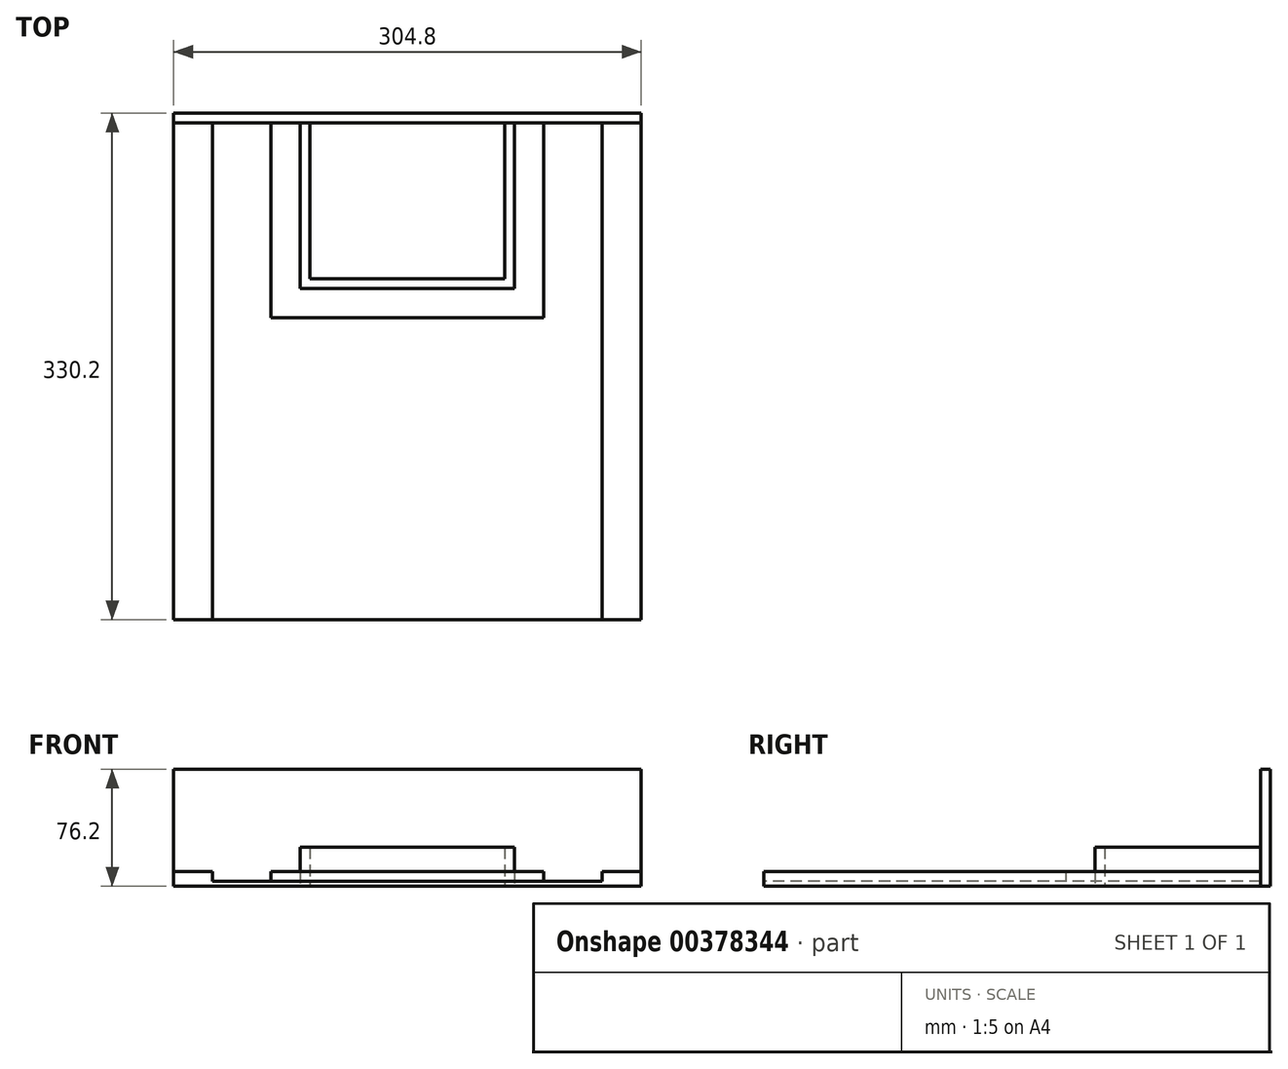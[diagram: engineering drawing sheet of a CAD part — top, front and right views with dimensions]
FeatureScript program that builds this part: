
annotation { "Feature Type Name" : "Feature", "Feature Type Description" : "" }
export const myFeature = defineFeature(function(context is Context, id is Id, definition is map)
    precondition{}
    {
        {
            var Q0;
            Q0=qCreatedBy(makeId("Top.planeOp"),FACE);
            var sketch = newSketch(context, id + "F0", { "sketchPlane" : qUnion([Q0])});
            skLineSegment(sketch, "E0.bottom", {"start": v(152.4, 165.1) * mm, "end": v(-152.4, 165.1) * mm});
            skLineSegment(sketch, "E0.top", {"start": v(152.4, -165.1) * mm, "end": v(-152.4, -165.1) * mm});
            skLineSegment(sketch, "E0.left", {"start": v(152.4, 165.1) * mm, "end": v(152.4, -165.1) * mm});
            skLineSegment(sketch, "E0.right", {"start": v(-152.4, 165.1) * mm, "end": v(-152.4, -165.1) * mm});
            skPoint(sketch, "E0.middle", {"position": v(0, 0) * mm});
            skLineSegment(sketch, "E1.0", {"start": v(152.4, 158.75) * mm, "end": v(-152.4, 158.75) * mm});
            skLineSegment(sketch, "E2.0", {"start": v(-127, 158.75) * mm, "end": v(-127, -165.1) * mm});
            skLineSegment(sketch, "E3.0", {"start": v(127, 158.75) * mm, "end": v(127, -165.1) * mm});
            skPoint(sketch, "E4", {"position": v(0, 158.75) * mm});
            skLineSegment(sketch, "E5", {"start": v(0, 158.75) * mm, "end": v(0, 0) * mm, "construction": true});
            skPoint(sketch, "E6", {"position": v(0, 57.15) * mm});
            skPoint(sketch, "E7", {"position": v(63.5, 57.15) * mm});
            skPoint(sketch, "E8", {"position": v(-63.5, 158.75) * mm});
            skLineSegment(sketch, "E9.bottom", {"start": v(-63.5, 158.75) * mm, "end": v(63.5, 158.75) * mm});
            skLineSegment(sketch, "E9.top", {"start": v(-63.5, 57.15) * mm, "end": v(63.5, 57.15) * mm});
            skLineSegment(sketch, "E9.left", {"start": v(-63.5, 158.75) * mm, "end": v(-63.5, 57.15) * mm});
            skLineSegment(sketch, "E9.right", {"start": v(63.5, 158.75) * mm, "end": v(63.5, 57.15) * mm});
            skLineSegment(sketch, "E10.0", {"start": v(-88.9, 31.75) * mm, "end": v(88.9, 31.75) * mm});
            skLineSegment(sketch, "E11.0", {"start": v(-88.9, 158.75) * mm, "end": v(-88.9, 31.75) * mm});
            skLineSegment(sketch, "E12.0", {"start": v(88.9, 158.75) * mm, "end": v(88.9, 31.75) * mm});
            skPoint(sketch, "E13", {"position": v(-88.9, 31.75) * mm});
            skPoint(sketch, "E14", {"position": v(88.9, 31.75) * mm});
            skPoint(sketch, "E15", {"position": v(-152.4, 158.75) * mm});
            skPoint(sketch, "E16", {"position": v(152.4, 158.75) * mm});
            skLineSegment(sketch, "E17.0", {"start": v(-69.85, 50.8) * mm, "end": v(69.85, 50.8) * mm});
            skLineSegment(sketch, "E18.0", {"start": v(69.85, 158.75) * mm, "end": v(69.85, 50.8) * mm});
            skLineSegment(sketch, "E19.0", {"start": v(-69.85, 158.75) * mm, "end": v(-69.85, 50.8) * mm});
            skPoint(sketch, "E20", {"position": v(-69.85, 50.8) * mm});
            skPoint(sketch, "E21", {"position": v(69.85, 50.8) * mm});
            skLineSegment(sketch, "E22", {"start": v(-88.9, 31.75) * mm, "end": v(-63.5, 57.15) * mm});
            skLineSegment(sketch, "E23", {"start": v(63.5, 57.15) * mm, "end": v(88.9, 31.75) * mm});
            skPoint(sketch, "E24", {"position": v(0, 107.95) * mm});
            skPoint(sketch, "E24.positionSnap0", {"position": v(63.5, 107.95) * mm});
            skSolve(sketch);
        }
        {
            var Q0;
            {var subQ0=sQuery(id+"F0.wireOp",EDGE,"E2.0");Q0=makeQuery(id+"F0.imprint","IMPRINT",FACE,{"disambiguationData":[TD([[makeQuery(id+"F0.imprint","IMPRINT",EDGE,{"derivedFrom":subQ0}),1.0]])]});}
            var Q1;
            Q1=makeQuery(id+"F0.imprint","IMPRINT",FACE,{"disambiguationData":[TD([[makeQuery(id+"F0.imprint","IMPRINT",EDGE,{"derivedFrom":sQuery(id+"F0.wireOp",EDGE,"E9.bottom")}),-1.0]])]});
            extrude(context, id + "F1", {"entities" : qUnion([Q0, Q1]), "depth" : 3.17 * mm});
        }
        {
            var Q0;
            {var subQ3=sQuery(id+"F0.wireOp",EDGE,"E3.0");Q0=makeQuery(id+"F0.imprint","IMPRINT",FACE,{"disambiguationData":[TD([[makeQuery(id+"F0.imprint","IMPRINT",EDGE,{"derivedFrom":subQ3}),1.0]])]});}
            var Q1;
            {var subQ0=sQuery(id+"F0.wireOp",EDGE,"E12.0");Q1=makeQuery(id+"F0.imprint","IMPRINT",FACE,{"disambiguationData":[TD([[makeQuery(id+"F0.imprint","IMPRINT",EDGE,{"derivedFrom":subQ0}),-1.0]])]});}
            var Q2;
            {var subQ0=sQuery(id+"F0.wireOp",EDGE,"E10.0");Q2=makeQuery(id+"F0.imprint","IMPRINT",FACE,{"disambiguationData":[TD([[makeQuery(id+"F0.imprint","IMPRINT",EDGE,{"derivedFrom":subQ0}),1.0]])]});}
            var Q3;
            {var subQ0=sQuery(id+"F0.wireOp",EDGE,"E11.0");Q3=makeQuery(id+"F0.imprint","IMPRINT",FACE,{"disambiguationData":[TD([[makeQuery(id+"F0.imprint","IMPRINT",EDGE,{"derivedFrom":subQ0}),1.0]])]});}
            var Q4;
            {var subQ3=sQuery(id+"F0.wireOp",EDGE,"E2.0");Q4=makeQuery(id+"F0.imprint","IMPRINT",FACE,{"disambiguationData":[TD([[makeQuery(id+"F0.imprint","IMPRINT",EDGE,{"derivedFrom":subQ3}),-1.0]])]});}
            extrude(context, id + "F2", {"entities" : qUnion([Q0, Q1, Q2, Q3, Q4]), "operationType" : NewBodyOperationType.ADD, "depth" : 9.52 * mm});
        }
        {
            var Q0;
            {var subQ0=sQuery(id+"F0.wireOp",EDGE,"E9.left");Q0=makeQuery(id+"F0.imprint","IMPRINT",FACE,{"disambiguationData":[TD([[makeQuery(id+"F0.imprint","IMPRINT",EDGE,{"derivedFrom":subQ0}),-1.0]])]});}
            var Q1;
            {var subQ0=sQuery(id+"F0.wireOp",EDGE,"E9.top");Q1=makeQuery(id+"F0.imprint","IMPRINT",FACE,{"disambiguationData":[TD([[makeQuery(id+"F0.imprint","IMPRINT",EDGE,{"derivedFrom":subQ0}),-1.0]])]});}
            var Q2;
            {var subQ0=sQuery(id+"F0.wireOp",EDGE,"E9.right");Q2=makeQuery(id+"F0.imprint","IMPRINT",FACE,{"disambiguationData":[TD([[makeQuery(id+"F0.imprint","IMPRINT",EDGE,{"derivedFrom":subQ0}),1.0]])]});}
            extrude(context, id + "F3", {"entities" : qUnion([Q0, Q1, Q2]), "depth" : 25.4 * mm});
        }
        {
            var Q0;
            {var subQ8=sQuery(id+"F0.wireOp",EDGE,"E0.bottom");Q0=makeQuery(id+"F0.imprint","IMPRINT",FACE,{"disambiguationData":[TD([[makeQuery(id+"F0.imprint","IMPRINT",EDGE,{"derivedFrom":subQ8}),1.0]])]});}
            extrude(context, id + "F4", {"entities" : qUnion([Q0]), "depth" : 76.2 * mm});
        }
    });
